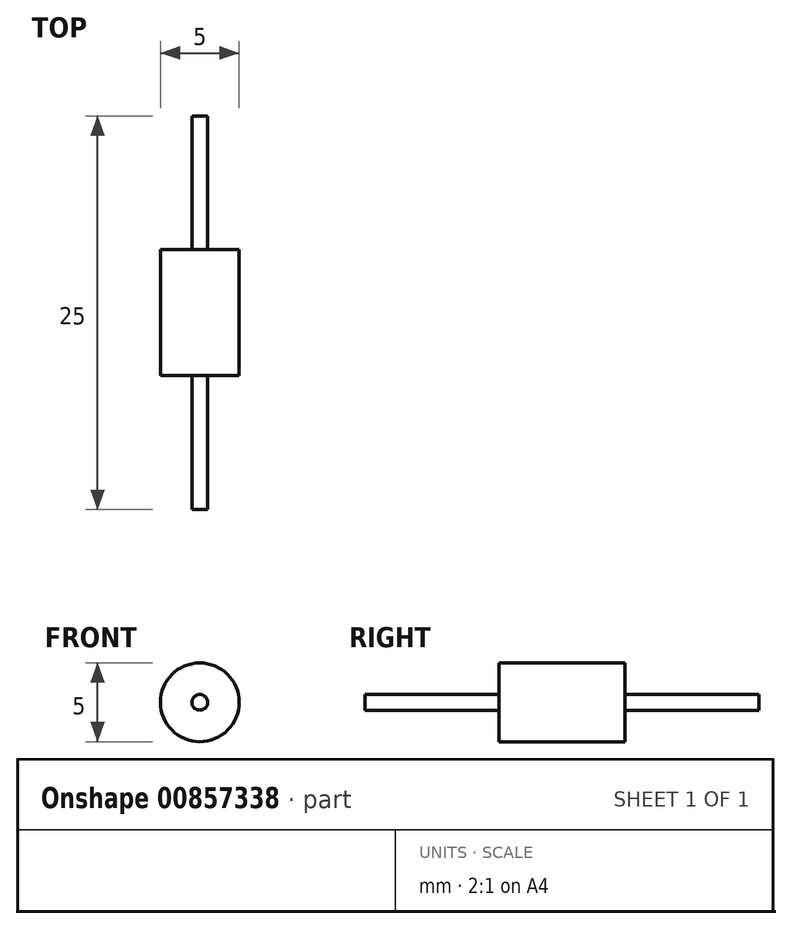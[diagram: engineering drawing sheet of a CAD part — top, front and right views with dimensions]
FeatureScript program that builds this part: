
annotation { "Feature Type Name" : "Feature", "Feature Type Description" : "" }
export const myFeature = defineFeature(function(context is Context, id is Id, definition is map)
    precondition{}
    {
        {
            var Q0;
            Q0=qCreatedBy(makeId("Front.planeOp"),FACE);
            var sketch = newSketch(context, id + "F0", { "sketchPlane" : qUnion([Q0])});
            skLineSegment(sketch, "E0.bottom", {"start": v(16, -16) * mm, "end": v(-16, -16) * mm});
            skLineSegment(sketch, "E0.top", {"start": v(16, 16) * mm, "end": v(-16, 16) * mm});
            skLineSegment(sketch, "E0.left", {"start": v(16, -16) * mm, "end": v(16, 16) * mm});
            skLineSegment(sketch, "E0.right", {"start": v(-16, -16) * mm, "end": v(-16, 16) * mm});
            skPoint(sketch, "E0.middle", {"position": v(0, 0) * mm});
            skCircle(sketch, "E1", {"center": v(0, 16) * mm, "radius": 2.5 * mm});
            skSolve(sketch);
        }
        {
            var Q0;
            {var subQ0=sQuery(id+"F0.wireOp",EDGE,"E1");var subQ1=sQuery(id+"F0.wireOp",EDGE,"E0.top");var subQ2=makeQuery(id+"F0.imprint","INTERSECT",VERTEX,{"disambiguationData":[OD(0.0)],"derivedFrom":[subQ1,subQ0]});Q0=makeQuery(id+"F0.imprint","IMPRINT",FACE,{"disambiguationData":[TD([[makeQuery(id+"F0.imprint","IMPRINT",EDGE,{"disambiguationData":[TD([[subQ2,-1.0]])],"derivedFrom":subQ1}),-1.0]])]});}
            var Q1;
            {var subQ0=sQuery(id+"F0.wireOp",EDGE,"E1");var subQ1=sQuery(id+"F0.wireOp",EDGE,"E0.top");var subQ2=makeQuery(id+"F0.imprint","INTERSECT",VERTEX,{"disambiguationData":[OD(0.0)],"derivedFrom":[subQ1,subQ0]});Q1=makeQuery(id+"F0.imprint","IMPRINT",FACE,{"disambiguationData":[TD([[makeQuery(id+"F0.imprint","IMPRINT",EDGE,{"disambiguationData":[TD([[subQ2,-1.0]])],"derivedFrom":subQ1}),1.0]])]});}
            extrude(context, id + "F1", {"entities" : qUnion([Q0, Q1]), "endBound" : BoundingType.SYMMETRIC, "depth" : 8 * mm, "offsetDistance" : 25 * mm});
        }
        {
            var Q0;
            Q0=qCreatedBy(makeId("Front.planeOp"),FACE);
            cPlane(context, id + "F2", {"entities" : qUnion([Q0]), "cplaneType" : CPlaneType.OFFSET, "offset" : 4 * mm, "width" : 150 * mm, "height" : 150 * mm});
        }
        {
            var Q0;
            Q0=qCreatedBy(id+"F2.planeOp",FACE);
            var sketch = newSketch(context, id + "F3", { "sketchPlane" : qUnion([Q0])});
            skLineSegment(sketch, "E2", {"start": v(0, 0) * mm, "end": v(0, 16) * mm});
            skCircle(sketch, "E3", {"center": v(0, 16) * mm, "radius": 0.5 * mm});
            skSolve(sketch);
        }
        {
            var Q0;
            Q0=makeQuery(id+"F3.imprint","IMPRINT",FACE,{"disambiguationData":[TD([[makeQuery(id+"F3.imprint","IMPRINT",EDGE,{"derivedFrom":sQuery(id+"F3.wireOp",EDGE,"E3")}),1.0]])]});
            var Q1;
            Q1 = qSketchRegion(id + "F3", true);
            extrude(context, id + "F4", {"entities" : qUnion([Q0, Q1]), "operationType" : NewBodyOperationType.REMOVE, "oppositeDirection" : true, "depth" : 25 * mm, "offsetDistance" : 25 * mm});
        }
        {
            var Q0;
            Q0=qCreatedBy(makeId("Front.planeOp"),FACE);
            var sketch = newSketch(context, id + "F5", { "sketchPlane" : qUnion([Q0])});
            skLineSegment(sketch, "E4", {"start": v(0, 0) * mm, "end": v(0, 16) * mm, "construction": true});
            skCircle(sketch, "E5", {"center": v(0, 16) * mm, "radius": 0.5 * mm});
            skSolve(sketch);
        }
        {
            var Q0;
            Q0 = qSketchRegion(id + "F5", true);
            extrude(context, id + "F6", {"entities" : qUnion([Q0]), "operationType" : NewBodyOperationType.ADD, "endBound" : BoundingType.SYMMETRIC, "depth" : 25 * mm, "offsetDistance" : 25 * mm});
        }
    });
